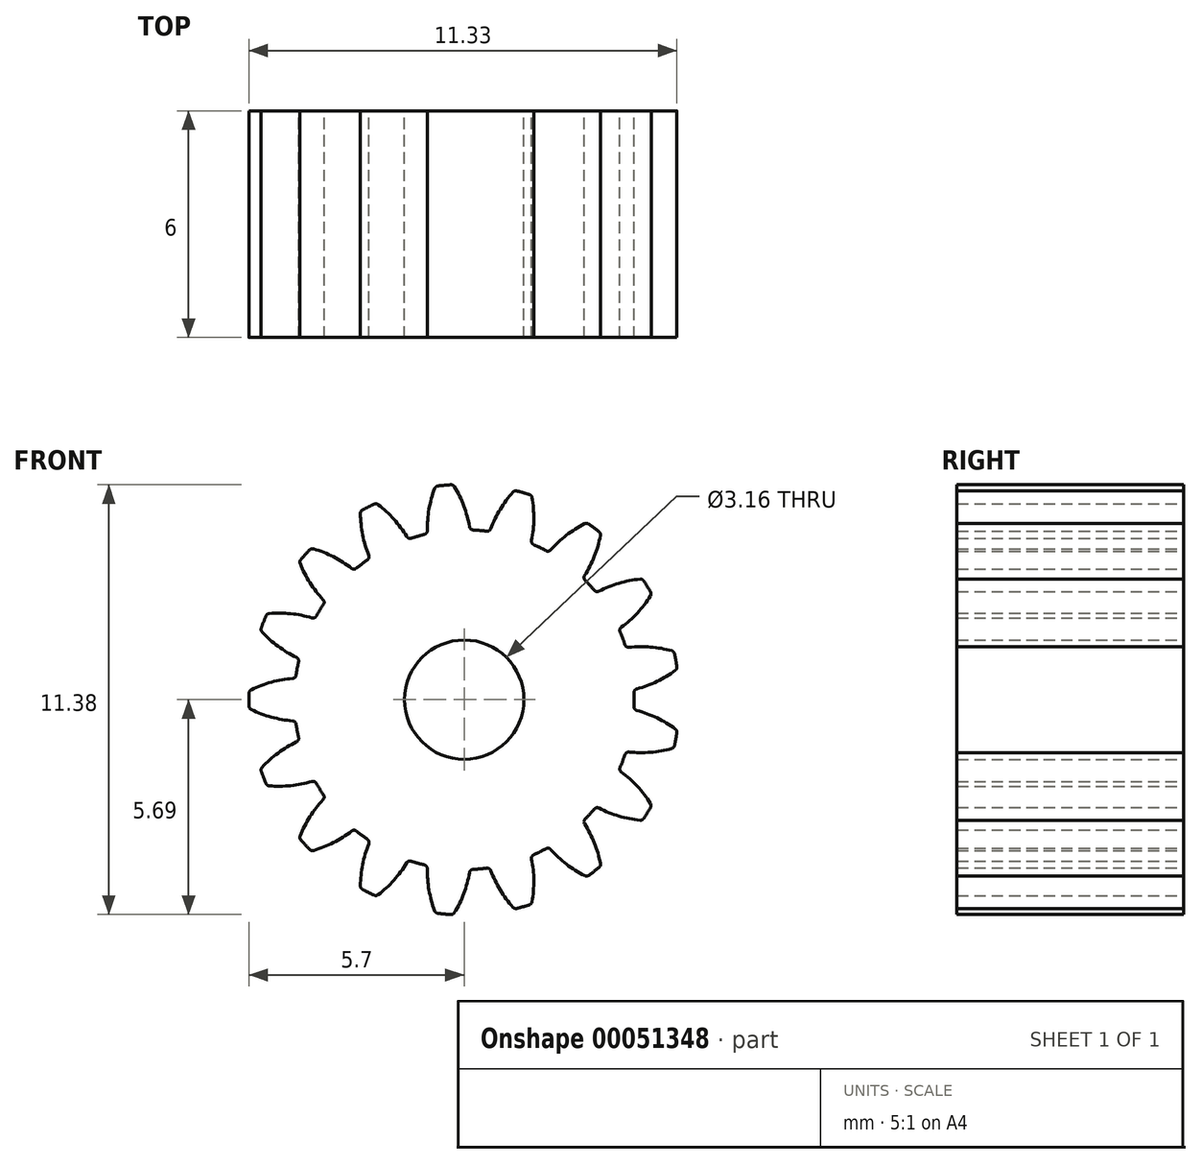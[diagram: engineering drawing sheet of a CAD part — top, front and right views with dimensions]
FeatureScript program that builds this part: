
annotation { "Feature Type Name" : "Feature", "Feature Type Description" : "" }
export const myFeature = defineFeature(function(context is Context, id is Id, definition is map)
    precondition{}
    {
        {
            var Q0;
            Q0=qCreatedBy(makeId("Front.planeOp"),FACE);
            var sketch = newSketch(context, id + "F0", { "sketchPlane" : qUnion([Q0])});
            skLineSegment(sketch, "E0", {"start": v(0, 0) * mm, "end": v(0, 8.7) * mm, "construction": true});
            skCircle(sketch, "E1", {"center": v(0, 0) * mm, "radius": 5.7 * mm, "construction": true});
            skCircle(sketch, "E2", {"center": v(0, 0) * mm, "radius": 5.1 * mm, "construction": true});
            skCircle(sketch, "E3", {"center": v(0, 0) * mm, "radius": 4.5 * mm, "construction": true});
            skLineSegment(sketch, "E4", {"start": v(0, 0) * mm, "end": v(-0.8, 8.58) * mm, "construction": true});
            skLineSegment(sketch, "E5", {"start": v(0, 5.1) * mm, "end": v(-6.72, 5.1) * mm, "construction": true});
            skLineSegment(sketch, "E6", {"start": v(0, 5.1) * mm, "end": v(-7.05, 2.54) * mm, "construction": true});
            skCircle(sketch, "E7", {"center": v(0, 5.1) * mm, "radius": 3.06 * mm, "construction": true});
            skCircle(sketch, "E8", {"center": v(-2.88, 4.05) * mm, "radius": 3.06 * mm, "construction": true});
            skArc(sketch, "E9", {"start": v(0.14, 4.58) * mm, "mid": v(-0.01, 5.13) * mm, "end": v(-0.26, 5.64) * mm});
            skArc(sketch, "E10.MirrorCS", {"start": v(-0.98, 4.47) * mm, "mid": v(-0.93, 5.04) * mm, "end": v(-0.78, 5.6) * mm});
            skArc(sketch, "E11", {"start": v(-0.35, 5.69) * mm, "mid": v(-0.53, 5.68) * mm, "end": v(-0.7, 5.66) * mm});
            skArc(sketch, "E12", {"start": v(0.23, 4.5) * mm, "mid": v(0.42, -4.48) * mm, "end": v(-1.06, 4.37) * mm});
            skPoint(sketch, "E13.visualSharp", {"position": v(-0.98, 4.4) * mm});
            skArc(sketch, "E13.filletArc", {"start": v(-1.06, 4.37) * mm, "mid": v(-1, 4.41) * mm, "end": v(-0.98, 4.47) * mm});
            skPoint(sketch, "E14.visualSharp", {"position": v(-0.76, 5.65) * mm});
            skArc(sketch, "E14.filletArc", {"start": v(-0.7, 5.66) * mm, "mid": v(-0.75, 5.64) * mm, "end": v(-0.78, 5.6) * mm});
            skPoint(sketch, "E15.visualSharp", {"position": v(-0.3, 5.7) * mm});
            skArc(sketch, "E15.filletArc", {"start": v(-0.26, 5.64) * mm, "mid": v(-0.3, 5.68) * mm, "end": v(-0.35, 5.69) * mm});
            skPoint(sketch, "E16.visualSharp", {"position": v(0.15, 4.5) * mm});
            skArc(sketch, "E16.filletArc", {"start": v(0.14, 4.58) * mm, "mid": v(0.17, 4.52) * mm, "end": v(0.23, 4.5) * mm});
            skArc(sketch, "E17.1.0", {"start": v(-2.56, 3.7) * mm, "mid": v(-2.53, 3.75) * mm, "end": v(-2.53, 3.82) * mm});
            skArc(sketch, "E17.1.1", {"start": v(-2.53, 3.82) * mm, "mid": v(-2.7, 4.37) * mm, "end": v(-2.75, 4.93) * mm});
            skArc(sketch, "E17.1.2", {"start": v(-2.7, 5.02) * mm, "mid": v(-2.73, 4.98) * mm, "end": v(-2.75, 4.93) * mm});
            skArc(sketch, "E17.1.3", {"start": v(-2.38, 5.18) * mm, "mid": v(-2.54, 5.1) * mm, "end": v(-2.7, 5.02) * mm});
            skArc(sketch, "E17.1.4", {"start": v(-2.28, 5.17) * mm, "mid": v(-2.33, 5.19) * mm, "end": v(-2.38, 5.18) * mm});
            skArc(sketch, "E17.1.5", {"start": v(-1.52, 4.32) * mm, "mid": v(-1.86, 4.78) * mm, "end": v(-2.28, 5.17) * mm});
            skArc(sketch, "E17.1.6", {"start": v(-1.52, 4.32) * mm, "mid": v(-1.47, 4.28) * mm, "end": v(-1.4, 4.28) * mm});
            skArc(sketch, "E17.2.0", {"start": v(-3.73, 2.52) * mm, "mid": v(-3.71, 2.59) * mm, "end": v(-3.74, 2.65) * mm});
            skArc(sketch, "E17.2.1", {"start": v(-3.74, 2.65) * mm, "mid": v(-4.09, 3.1) * mm, "end": v(-4.34, 3.6) * mm});
            skArc(sketch, "E17.2.2", {"start": v(-4.33, 3.7) * mm, "mid": v(-4.35, 3.66) * mm, "end": v(-4.34, 3.6) * mm});
            skArc(sketch, "E17.2.3", {"start": v(-4.1, 3.97) * mm, "mid": v(-4.21, 3.84) * mm, "end": v(-4.33, 3.7) * mm});
            skArc(sketch, "E17.2.4", {"start": v(-4, 4) * mm, "mid": v(-4.05, 4) * mm, "end": v(-4.1, 3.97) * mm});
            skArc(sketch, "E17.2.5", {"start": v(-2.98, 3.48) * mm, "mid": v(-3.46, 3.78) * mm, "end": v(-4, 4) * mm});
            skArc(sketch, "E17.2.6", {"start": v(-2.98, 3.48) * mm, "mid": v(-2.92, 3.46) * mm, "end": v(-2.85, 3.48) * mm});
            skArc(sketch, "E17.3.0", {"start": v(-4.39, 1) * mm, "mid": v(-4.4, 1.07) * mm, "end": v(-4.44, 1.12) * mm});
            skArc(sketch, "E17.3.1", {"start": v(-4.44, 1.12) * mm, "mid": v(-4.93, 1.41) * mm, "end": v(-5.35, 1.8) * mm});
            skArc(sketch, "E17.3.2", {"start": v(-5.38, 1.9) * mm, "mid": v(-5.38, 1.84) * mm, "end": v(-5.35, 1.8) * mm});
            skArc(sketch, "E17.3.3", {"start": v(-5.25, 2.22) * mm, "mid": v(-5.32, 2.06) * mm, "end": v(-5.38, 1.9) * mm});
            skArc(sketch, "E17.3.4", {"start": v(-5.16, 2.28) * mm, "mid": v(-5.22, 2.26) * mm, "end": v(-5.25, 2.22) * mm});
            skArc(sketch, "E17.3.5", {"start": v(-4.04, 2.17) * mm, "mid": v(-4.6, 2.28) * mm, "end": v(-5.16, 2.28) * mm});
            skArc(sketch, "E17.3.6", {"start": v(-4.04, 2.17) * mm, "mid": v(-3.97, 2.17) * mm, "end": v(-3.92, 2.21) * mm});
            skArc(sketch, "E17.4.0", {"start": v(-4.45, -0.65) * mm, "mid": v(-4.48, -0.59) * mm, "end": v(-4.55, -0.56) * mm});
            skArc(sketch, "E17.4.1", {"start": v(-4.55, -0.56) * mm, "mid": v(-5.1, -0.46) * mm, "end": v(-5.64, -0.26) * mm});
            skArc(sketch, "E17.4.2", {"start": v(-5.7, -0.17) * mm, "mid": v(-5.68, -0.23) * mm, "end": v(-5.64, -0.26) * mm});
            skArc(sketch, "E17.4.3", {"start": v(-5.7, 0.17) * mm, "mid": v(-5.7, 0) * mm, "end": v(-5.7, -0.17) * mm});
            skArc(sketch, "E17.4.4", {"start": v(-5.64, 0.26) * mm, "mid": v(-5.68, 0.23) * mm, "end": v(-5.7, 0.17) * mm});
            skArc(sketch, "E17.4.5", {"start": v(-4.55, 0.56) * mm, "mid": v(-5.1, 0.46) * mm, "end": v(-5.64, 0.26) * mm});
            skArc(sketch, "E17.4.6", {"start": v(-4.55, 0.56) * mm, "mid": v(-4.48, 0.59) * mm, "end": v(-4.45, 0.65) * mm});
            skArc(sketch, "E17.5.0", {"start": v(-3.92, -2.21) * mm, "mid": v(-3.97, -2.17) * mm, "end": v(-4.04, -2.17) * mm});
            skArc(sketch, "E17.5.1", {"start": v(-4.04, -2.17) * mm, "mid": v(-4.6, -2.28) * mm, "end": v(-5.16, -2.28) * mm});
            skArc(sketch, "E17.5.2", {"start": v(-5.25, -2.22) * mm, "mid": v(-5.22, -2.26) * mm, "end": v(-5.16, -2.28) * mm});
            skArc(sketch, "E17.5.3", {"start": v(-5.38, -1.9) * mm, "mid": v(-5.32, -2.06) * mm, "end": v(-5.25, -2.22) * mm});
            skArc(sketch, "E17.5.4", {"start": v(-5.35, -1.8) * mm, "mid": v(-5.38, -1.84) * mm, "end": v(-5.38, -1.9) * mm});
            skArc(sketch, "E17.5.5", {"start": v(-4.44, -1.12) * mm, "mid": v(-4.93, -1.41) * mm, "end": v(-5.35, -1.8) * mm});
            skArc(sketch, "E17.5.6", {"start": v(-4.44, -1.12) * mm, "mid": v(-4.4, -1.07) * mm, "end": v(-4.39, -1) * mm});
            skArc(sketch, "E17.6.0", {"start": v(-2.85, -3.48) * mm, "mid": v(-2.92, -3.46) * mm, "end": v(-2.98, -3.48) * mm});
            skArc(sketch, "E17.6.1", {"start": v(-2.98, -3.48) * mm, "mid": v(-3.46, -3.78) * mm, "end": v(-4, -4) * mm});
            skArc(sketch, "E17.6.2", {"start": v(-4.1, -3.97) * mm, "mid": v(-4.05, -4) * mm, "end": v(-4, -4) * mm});
            skArc(sketch, "E17.6.3", {"start": v(-4.33, -3.7) * mm, "mid": v(-4.21, -3.84) * mm, "end": v(-4.1, -3.97) * mm});
            skArc(sketch, "E17.6.4", {"start": v(-4.34, -3.6) * mm, "mid": v(-4.35, -3.66) * mm, "end": v(-4.33, -3.7) * mm});
            skArc(sketch, "E17.6.5", {"start": v(-3.74, -2.65) * mm, "mid": v(-4.09, -3.1) * mm, "end": v(-4.34, -3.6) * mm});
            skArc(sketch, "E17.6.6", {"start": v(-3.74, -2.65) * mm, "mid": v(-3.71, -2.59) * mm, "end": v(-3.73, -2.52) * mm});
            skArc(sketch, "E17.7.0", {"start": v(-1.4, -4.28) * mm, "mid": v(-1.47, -4.28) * mm, "end": v(-1.52, -4.32) * mm});
            skArc(sketch, "E17.7.1", {"start": v(-1.52, -4.32) * mm, "mid": v(-1.86, -4.78) * mm, "end": v(-2.28, -5.17) * mm});
            skArc(sketch, "E17.7.2", {"start": v(-2.38, -5.18) * mm, "mid": v(-2.33, -5.19) * mm, "end": v(-2.28, -5.17) * mm});
            skArc(sketch, "E17.7.3", {"start": v(-2.7, -5.02) * mm, "mid": v(-2.54, -5.1) * mm, "end": v(-2.38, -5.18) * mm});
            skArc(sketch, "E17.7.4", {"start": v(-2.75, -4.93) * mm, "mid": v(-2.73, -4.98) * mm, "end": v(-2.7, -5.02) * mm});
            skArc(sketch, "E17.7.5", {"start": v(-2.53, -3.82) * mm, "mid": v(-2.7, -4.37) * mm, "end": v(-2.75, -4.93) * mm});
            skArc(sketch, "E17.7.6", {"start": v(-2.53, -3.82) * mm, "mid": v(-2.53, -3.75) * mm, "end": v(-2.56, -3.7) * mm});
            skArc(sketch, "E17.8.0", {"start": v(0.23, -4.5) * mm, "mid": v(0.17, -4.52) * mm, "end": v(0.14, -4.58) * mm});
            skArc(sketch, "E17.8.1", {"start": v(0.14, -4.58) * mm, "mid": v(-0.01, -5.13) * mm, "end": v(-0.26, -5.64) * mm});
            skArc(sketch, "E17.8.2", {"start": v(-0.35, -5.69) * mm, "mid": v(-0.3, -5.68) * mm, "end": v(-0.26, -5.64) * mm});
            skArc(sketch, "E17.8.3", {"start": v(-0.7, -5.66) * mm, "mid": v(-0.53, -5.68) * mm, "end": v(-0.35, -5.69) * mm});
            skArc(sketch, "E17.8.4", {"start": v(-0.78, -5.6) * mm, "mid": v(-0.75, -5.64) * mm, "end": v(-0.7, -5.66) * mm});
            skArc(sketch, "E17.8.5", {"start": v(-0.98, -4.47) * mm, "mid": v(-0.93, -5.04) * mm, "end": v(-0.78, -5.6) * mm});
            skArc(sketch, "E17.8.6", {"start": v(-0.98, -4.47) * mm, "mid": v(-1, -4.41) * mm, "end": v(-1.06, -4.37) * mm});
            skArc(sketch, "E17.9.0", {"start": v(1.84, -4.1) * mm, "mid": v(1.8, -4.15) * mm, "end": v(1.78, -4.22) * mm});
            skArc(sketch, "E17.9.1", {"start": v(1.78, -4.22) * mm, "mid": v(1.84, -4.79) * mm, "end": v(1.8, -5.35) * mm});
            skArc(sketch, "E17.9.2", {"start": v(1.73, -5.43) * mm, "mid": v(1.77, -5.4) * mm, "end": v(1.8, -5.35) * mm});
            skArc(sketch, "E17.9.3", {"start": v(1.4, -5.53) * mm, "mid": v(1.56, -5.48) * mm, "end": v(1.73, -5.43) * mm});
            skArc(sketch, "E17.9.4", {"start": v(1.3, -5.5) * mm, "mid": v(1.34, -5.53) * mm, "end": v(1.4, -5.53) * mm});
            skArc(sketch, "E17.9.5", {"start": v(0.7, -4.53) * mm, "mid": v(0.95, -5.04) * mm, "end": v(1.3, -5.5) * mm});
            skArc(sketch, "E17.9.6", {"start": v(0.7, -4.53) * mm, "mid": v(0.66, -4.47) * mm, "end": v(0.6, -4.46) * mm});
            skArc(sketch, "E17.10.0", {"start": v(3.2, -3.16) * mm, "mid": v(3.17, -3.22) * mm, "end": v(3.19, -3.29) * mm});
            skArc(sketch, "E17.10.1", {"start": v(3.19, -3.29) * mm, "mid": v(3.45, -3.8) * mm, "end": v(3.6, -4.34) * mm});
            skArc(sketch, "E17.10.2", {"start": v(3.57, -4.44) * mm, "mid": v(3.6, -4.4) * mm, "end": v(3.6, -4.34) * mm});
            skArc(sketch, "E17.10.3", {"start": v(3.3, -4.65) * mm, "mid": v(3.44, -4.55) * mm, "end": v(3.57, -4.44) * mm});
            skArc(sketch, "E17.10.4", {"start": v(3.19, -4.66) * mm, "mid": v(3.24, -4.67) * mm, "end": v(3.3, -4.65) * mm});
            skArc(sketch, "E17.10.5", {"start": v(2.3, -3.97) * mm, "mid": v(2.7, -4.35) * mm, "end": v(3.19, -4.66) * mm});
            skArc(sketch, "E17.10.6", {"start": v(2.3, -3.97) * mm, "mid": v(2.23, -3.93) * mm, "end": v(2.17, -3.94) * mm});
            skArc(sketch, "E17.11.0", {"start": v(4.13, -1.8) * mm, "mid": v(4.12, -1.86) * mm, "end": v(4.16, -1.92) * mm});
            skArc(sketch, "E17.11.1", {"start": v(4.16, -1.92) * mm, "mid": v(4.59, -2.3) * mm, "end": v(4.93, -2.75) * mm});
            skArc(sketch, "E17.11.2", {"start": v(4.94, -2.85) * mm, "mid": v(4.95, -2.8) * mm, "end": v(4.93, -2.75) * mm});
            skArc(sketch, "E17.11.3", {"start": v(4.75, -3.15) * mm, "mid": v(4.85, -3) * mm, "end": v(4.94, -2.85) * mm});
            skArc(sketch, "E17.11.4", {"start": v(4.66, -3.2) * mm, "mid": v(4.71, -3.18) * mm, "end": v(4.75, -3.15) * mm});
            skArc(sketch, "E17.11.5", {"start": v(3.57, -2.87) * mm, "mid": v(4.1, -3.08) * mm, "end": v(4.66, -3.2) * mm});
            skArc(sketch, "E17.11.6", {"start": v(3.57, -2.87) * mm, "mid": v(3.5, -2.86) * mm, "end": v(3.44, -2.9) * mm});
            skArc(sketch, "E17.12.0", {"start": v(4.5, -0.18) * mm, "mid": v(4.52, -0.25) * mm, "end": v(4.57, -0.28) * mm});
            skArc(sketch, "E17.12.1", {"start": v(4.57, -0.28) * mm, "mid": v(5.1, -0.48) * mm, "end": v(5.6, -0.78) * mm});
            skArc(sketch, "E17.12.2", {"start": v(5.63, -0.88) * mm, "mid": v(5.63, -0.82) * mm, "end": v(5.6, -0.78) * mm});
            skArc(sketch, "E17.12.3", {"start": v(5.57, -1.22) * mm, "mid": v(5.6, -1.05) * mm, "end": v(5.63, -0.88) * mm});
            skArc(sketch, "E17.12.4", {"start": v(5.5, -1.3) * mm, "mid": v(5.54, -1.27) * mm, "end": v(5.57, -1.22) * mm});
            skArc(sketch, "E17.12.5", {"start": v(4.37, -1.39) * mm, "mid": v(4.93, -1.4) * mm, "end": v(5.5, -1.3) * mm});
            skArc(sketch, "E17.12.6", {"start": v(4.37, -1.39) * mm, "mid": v(4.3, -1.4) * mm, "end": v(4.26, -1.46) * mm});
            skArc(sketch, "E17.13.0", {"start": v(4.26, 1.46) * mm, "mid": v(4.3, 1.4) * mm, "end": v(4.37, 1.39) * mm});
            skArc(sketch, "E17.13.1", {"start": v(4.37, 1.39) * mm, "mid": v(4.93, 1.4) * mm, "end": v(5.5, 1.3) * mm});
            skArc(sketch, "E17.13.2", {"start": v(5.57, 1.22) * mm, "mid": v(5.54, 1.27) * mm, "end": v(5.5, 1.3) * mm});
            skArc(sketch, "E17.13.3", {"start": v(5.63, 0.88) * mm, "mid": v(5.6, 1.05) * mm, "end": v(5.57, 1.22) * mm});
            skArc(sketch, "E17.13.4", {"start": v(5.6, 0.78) * mm, "mid": v(5.63, 0.82) * mm, "end": v(5.63, 0.88) * mm});
            skArc(sketch, "E17.13.5", {"start": v(4.57, 0.28) * mm, "mid": v(5.1, 0.48) * mm, "end": v(5.6, 0.78) * mm});
            skArc(sketch, "E17.13.6", {"start": v(4.57, 0.28) * mm, "mid": v(4.52, 0.25) * mm, "end": v(4.5, 0.18) * mm});
            skArc(sketch, "E17.14.0", {"start": v(3.44, 2.9) * mm, "mid": v(3.5, 2.86) * mm, "end": v(3.57, 2.87) * mm});
            skArc(sketch, "E17.14.1", {"start": v(3.57, 2.87) * mm, "mid": v(4.1, 3.08) * mm, "end": v(4.66, 3.2) * mm});
            skArc(sketch, "E17.14.2", {"start": v(4.75, 3.15) * mm, "mid": v(4.71, 3.18) * mm, "end": v(4.66, 3.2) * mm});
            skArc(sketch, "E17.14.3", {"start": v(4.94, 2.85) * mm, "mid": v(4.85, 3) * mm, "end": v(4.75, 3.15) * mm});
            skArc(sketch, "E17.14.4", {"start": v(4.93, 2.75) * mm, "mid": v(4.95, 2.8) * mm, "end": v(4.94, 2.85) * mm});
            skArc(sketch, "E17.14.5", {"start": v(4.16, 1.92) * mm, "mid": v(4.59, 2.3) * mm, "end": v(4.93, 2.75) * mm});
            skArc(sketch, "E17.14.6", {"start": v(4.16, 1.92) * mm, "mid": v(4.12, 1.86) * mm, "end": v(4.13, 1.8) * mm});
            skArc(sketch, "E17.15.0", {"start": v(2.17, 3.94) * mm, "mid": v(2.23, 3.93) * mm, "end": v(2.3, 3.97) * mm});
            skArc(sketch, "E17.15.1", {"start": v(2.3, 3.97) * mm, "mid": v(2.7, 4.35) * mm, "end": v(3.19, 4.66) * mm});
            skArc(sketch, "E17.15.2", {"start": v(3.3, 4.65) * mm, "mid": v(3.24, 4.67) * mm, "end": v(3.19, 4.66) * mm});
            skArc(sketch, "E17.15.3", {"start": v(3.57, 4.44) * mm, "mid": v(3.44, 4.55) * mm, "end": v(3.3, 4.65) * mm});
            skArc(sketch, "E17.15.4", {"start": v(3.6, 4.34) * mm, "mid": v(3.6, 4.4) * mm, "end": v(3.57, 4.44) * mm});
            skArc(sketch, "E17.15.5", {"start": v(3.19, 3.29) * mm, "mid": v(3.45, 3.8) * mm, "end": v(3.6, 4.34) * mm});
            skArc(sketch, "E17.15.6", {"start": v(3.19, 3.29) * mm, "mid": v(3.17, 3.22) * mm, "end": v(3.2, 3.16) * mm});
            skArc(sketch, "E17.16.0", {"start": v(0.6, 4.46) * mm, "mid": v(0.66, 4.47) * mm, "end": v(0.7, 4.53) * mm});
            skArc(sketch, "E17.16.1", {"start": v(0.7, 4.53) * mm, "mid": v(0.95, 5.04) * mm, "end": v(1.3, 5.5) * mm});
            skArc(sketch, "E17.16.2", {"start": v(1.4, 5.53) * mm, "mid": v(1.34, 5.53) * mm, "end": v(1.3, 5.5) * mm});
            skArc(sketch, "E17.16.3", {"start": v(1.73, 5.43) * mm, "mid": v(1.56, 5.48) * mm, "end": v(1.4, 5.53) * mm});
            skArc(sketch, "E17.16.4", {"start": v(1.8, 5.35) * mm, "mid": v(1.77, 5.4) * mm, "end": v(1.73, 5.43) * mm});
            skArc(sketch, "E17.16.5", {"start": v(1.78, 4.22) * mm, "mid": v(1.84, 4.79) * mm, "end": v(1.8, 5.35) * mm});
            skArc(sketch, "E17.16.6", {"start": v(1.78, 4.22) * mm, "mid": v(1.8, 4.15) * mm, "end": v(1.84, 4.1) * mm});
            skCircle(sketch, "E18", {"center": v(0, 0) * mm, "radius": 1.58 * mm});
            skSolve(sketch);
        }
        {
            var Q0;
            Q0 = qSketchRegion(id + "F0", true);
            extrude(context, id + "F1", {"entities" : qUnion([Q0]), "depth" : 6 * mm, "symmetric" : true});
        }
    });
